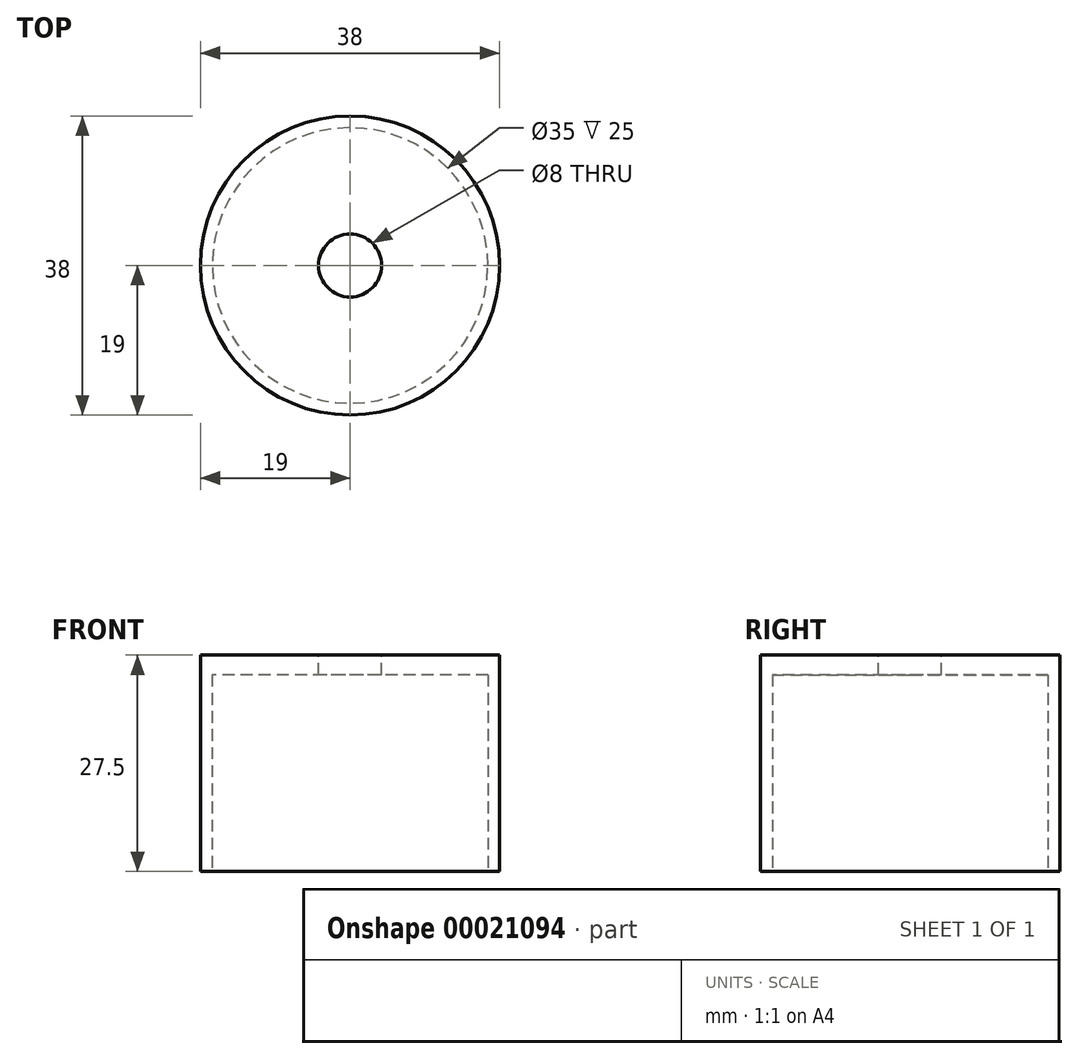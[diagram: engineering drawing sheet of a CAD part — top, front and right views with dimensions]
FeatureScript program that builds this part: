
annotation { "Feature Type Name" : "Feature", "Feature Type Description" : "" }
export const myFeature = defineFeature(function(context is Context, id is Id, definition is map)
    precondition{}
    {
        {
            var Q0;
            Q0=qCreatedBy(makeId("Top.planeOp"),FACE);
            var sketch = newSketch(context, id + "F0", { "sketchPlane" : qUnion([Q0])});
            skCircle(sketch, "E0", {"center": v(0, 0) * mm, "radius": 17.5 * mm});
            skCircle(sketch, "E1.0", {"center": v(0, 0) * mm, "radius": 19 * mm});
            skSolve(sketch);
        }
        {
            var Q0;
            Q0 = qSketchRegion(id + "F0", true);
            extrude(context, id + "F1", {"entities" : qUnion([Q0]), "depth" : 25 * mm});
        }
        {
            var Q0;
            Q0=makeQuery(id+"F1.opExtrude","CAP_FACE",FACE,{"disambiguationData":[OSD([sQuery(id+"F0.wireOp",EDGE,"E0"),sQuery(id+"F0.wireOp",EDGE,"E1.0")])],"isStart":false});
            var sketch = newSketch(context, id + "F2", { "sketchPlane" : qUnion([Q0])});
            skCircle(sketch, "E2", {"center": v(0, 0) * mm, "radius": 19 * mm});
            skSolve(sketch);
        }
        {
            var Q0;
            Q0 = qSketchRegion(id + "F2", true);
            extrude(context, id + "F3", {"entities" : qUnion([Q0]), "operationType" : NewBodyOperationType.ADD, "depth" : 2.5 * mm});
        }
        {
            var Q0;
            Q0=makeQuery(id+"F3.opExtrude","CAP_FACE",FACE,{"disambiguationData":[OSD([sQuery(id+"F2.wireOp",EDGE,"E2")])],"isStart":false});
            var sketch = newSketch(context, id + "F4", { "sketchPlane" : qUnion([Q0])});
            skCircle(sketch, "E3", {"center": v(0, 0) * mm, "radius": 4 * mm});
            skSolve(sketch);
        }
        {
            var Q0;
            Q0 = qSketchRegion(id + "F4", true);
            extrude(context, id + "F5", {"entities" : qUnion([Q0]), "operationType" : NewBodyOperationType.REMOVE, "endBound" : BoundingType.THROUGH_ALL, "oppositeDirection" : true, "depth" : 25 * mm});
        }
    });
